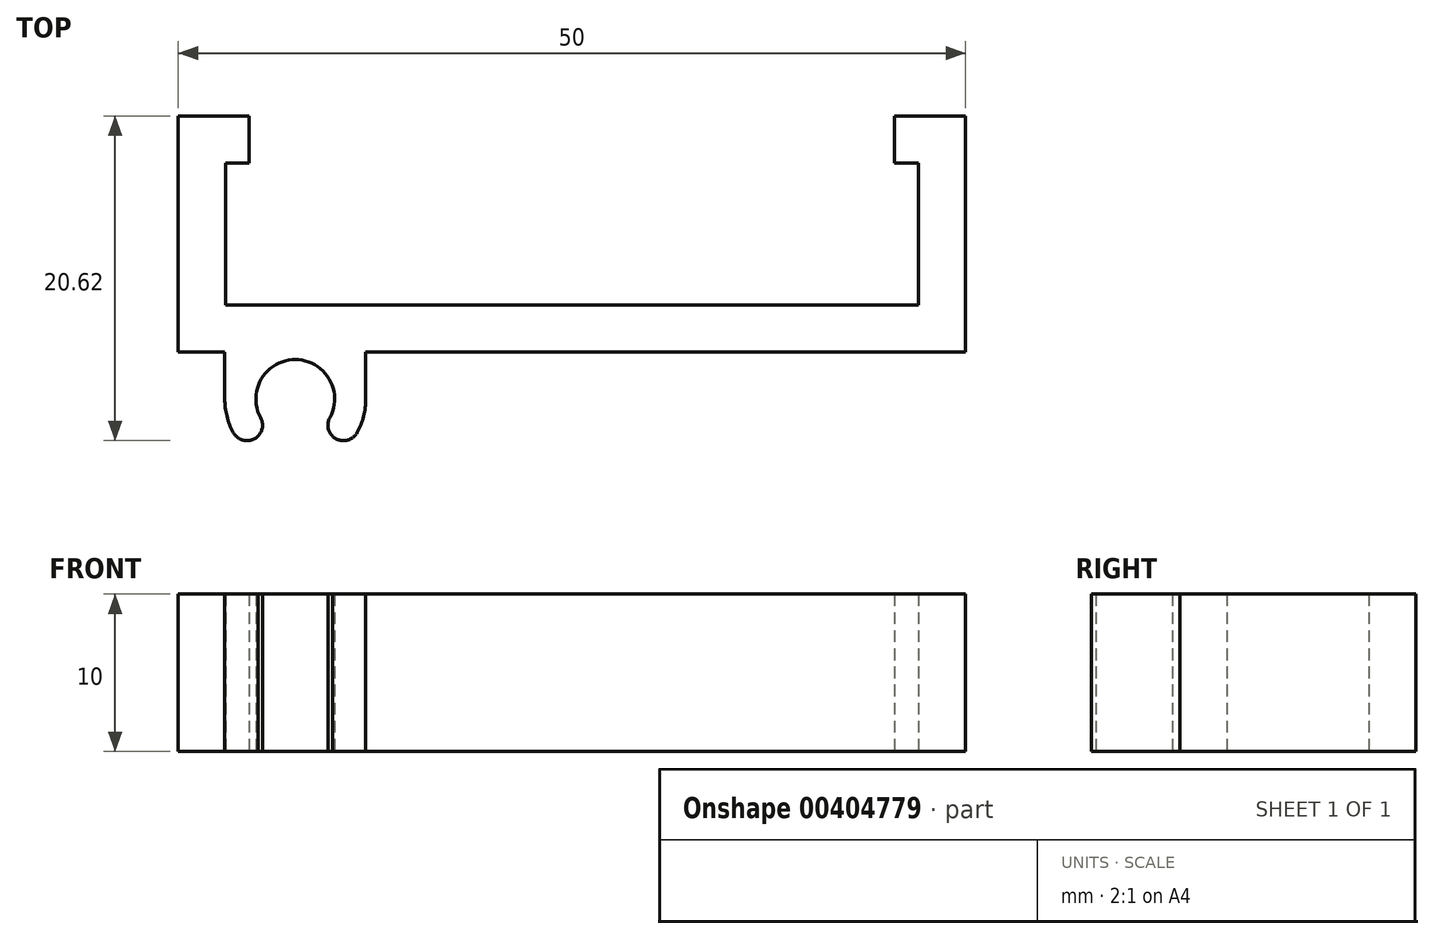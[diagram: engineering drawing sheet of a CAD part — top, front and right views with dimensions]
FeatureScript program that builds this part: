
annotation { "Feature Type Name" : "Feature", "Feature Type Description" : "" }
export const myFeature = defineFeature(function(context is Context, id is Id, definition is map)
    precondition{}
    {
        {
            var Q0;
            Q0=qCreatedBy(makeId("Top.planeOp"),FACE);
            var sketch = newSketch(context, id + "F0", { "sketchPlane" : qUnion([Q0])});
            skLineSegment(sketch, "E0", {"start": v(12.41, 0) * mm, "end": v(-25.68, 0) * mm});
            skLineSegment(sketch, "E1", {"start": v(-37.59, 0) * mm, "end": v(-37.59, 15) * mm});
            skLineSegment(sketch, "E2", {"start": v(-37.59, 15) * mm, "end": v(-33.09, 15) * mm});
            skLineSegment(sketch, "E3", {"start": v(-33.09, 15) * mm, "end": v(-33.09, 12) * mm});
            skLineSegment(sketch, "E4", {"start": v(-33.09, 12) * mm, "end": v(-34.59, 12) * mm});
            skLineSegment(sketch, "E5", {"start": v(-34.59, 12) * mm, "end": v(-34.59, 3) * mm});
            skLineSegment(sketch, "E6", {"start": v(-34.59, 3) * mm, "end": v(9.41, 3) * mm});
            skLineSegment(sketch, "E7", {"start": v(9.41, 3) * mm, "end": v(9.41, 12) * mm});
            skLineSegment(sketch, "E8", {"start": v(9.41, 12) * mm, "end": v(7.91, 12) * mm});
            skLineSegment(sketch, "E9", {"start": v(7.91, 12) * mm, "end": v(7.91, 15) * mm});
            skLineSegment(sketch, "E10", {"start": v(7.91, 15) * mm, "end": v(12.41, 15) * mm});
            skLineSegment(sketch, "E11", {"start": v(12.41, 15) * mm, "end": v(12.41, 0) * mm});
            skLineSegment(sketch, "E12", {"start": v(-30.16, -2.98) * mm, "end": v(-16.92, -2.98) * mm, "construction": true});
            skLineSegment(sketch, "E13", {"start": v(-30.16, -2.98) * mm, "end": v(-41.24, -2.98) * mm, "construction": true});
            skArc(sketch, "E14", {"start": v(-34.63, -2.98) * mm, "mid": v(-34.3, -4.69) * mm, "end": v(-33.32, -6.14) * mm});
            skLineSegment(sketch, "E15", {"start": v(-25.68, -2.98) * mm, "end": v(-25.68, 0) * mm});
            skLineSegment(sketch, "E16", {"start": v(-34.63, -2.98) * mm, "end": v(-34.63, 0) * mm});
            skLineSegment(sketch, "E17", {"start": v(-30.16, -2.98) * mm, "end": v(-30.16, 3.84) * mm, "construction": true});
            skLineSegment(sketch, "E18", {"start": v(-30.16, -2.98) * mm, "end": v(-30.16, -9.65) * mm, "construction": true});
            skArc(sketch, "E19", {"start": v(-30.16, -0.48) * mm, "mid": v(-32.46, -2.02) * mm, "end": v(-31.92, -4.74) * mm});
            skArc(sketch, "E20", {"start": v(-28.39, -4.74) * mm, "mid": v(-27.85, -2.02) * mm, "end": v(-30.16, -0.48) * mm});
            skArc(sketch, "E21", {"start": v(-26.99, -6.14) * mm, "mid": v(-26.02, -4.69) * mm, "end": v(-25.68, -2.98) * mm});
            skLineSegment(sketch, "E22", {"start": v(-31.92, -4.74) * mm, "end": v(-33.32, -6.14) * mm});
            skLineSegment(sketch, "E23", {"start": v(-28.39, -4.74) * mm, "end": v(-26.99, -6.14) * mm});
            skLineSegment(sketch, "E24", {"start": v(-34.63, 0) * mm, "end": v(-37.59, 0) * mm});
            skSolve(sketch);
        }
        {
            var Q0;
            {var subQ4=sQuery(id+"F0.wireOp",EDGE,"E1");Q0=makeQuery(id+"F0.imprint","IMPRINT",FACE,{"disambiguationData":[TD([[makeQuery(id+"F0.imprint","IMPRINT",EDGE,{"derivedFrom":subQ4}),-1.0]])]});}
            var Q1;
            Q1=makeQuery(id+"F0.imprint","IMPRINT",FACE,{"disambiguationData":[TD([[makeQuery(id+"F0.imprint","IMPRINT",EDGE,{"derivedFrom":sQuery(id+"F0.wireOp",EDGE,"E14")}),1.0]])]});
            extrude(context, id + "F1", {"entities" : qUnion([Q0, Q1]), "depth" : 10 * mm});
        }
        {
            var Q0;
            Q0=makeQuery(id+"F1.opExtrude","SWEPT_EDGE",EDGE,{"disambiguationData":[OSD([sQuery(id+"F0.wireOp",EDGE,"E14"),sQuery(id+"F0.wireOp",EDGE,"E22")])]});
            var Q1;
            Q1=makeQuery(id+"F1.opExtrude","SWEPT_EDGE",EDGE,{"disambiguationData":[OSD([sQuery(id+"F0.wireOp",EDGE,"E19"),sQuery(id+"F0.wireOp",EDGE,"E22")])]});
            var Q2;
            Q2=makeQuery(id+"F1.opExtrude","SWEPT_EDGE",EDGE,{"disambiguationData":[OSD([sQuery(id+"F0.wireOp",EDGE,"E20"),sQuery(id+"F0.wireOp",EDGE,"E23")])]});
            var Q3;
            Q3=makeQuery(id+"F1.opExtrude","SWEPT_EDGE",EDGE,{"disambiguationData":[OSD([sQuery(id+"F0.wireOp",EDGE,"E21"),sQuery(id+"F0.wireOp",EDGE,"E23")])]});
            fillet(context, id + "F2", {"entities" : qUnion([Q0, Q1, Q2, Q3]), "radius" : 1 * mm, "tangentPropagation" : true, "allowEdgeOverflow" : false});
        }
    });
